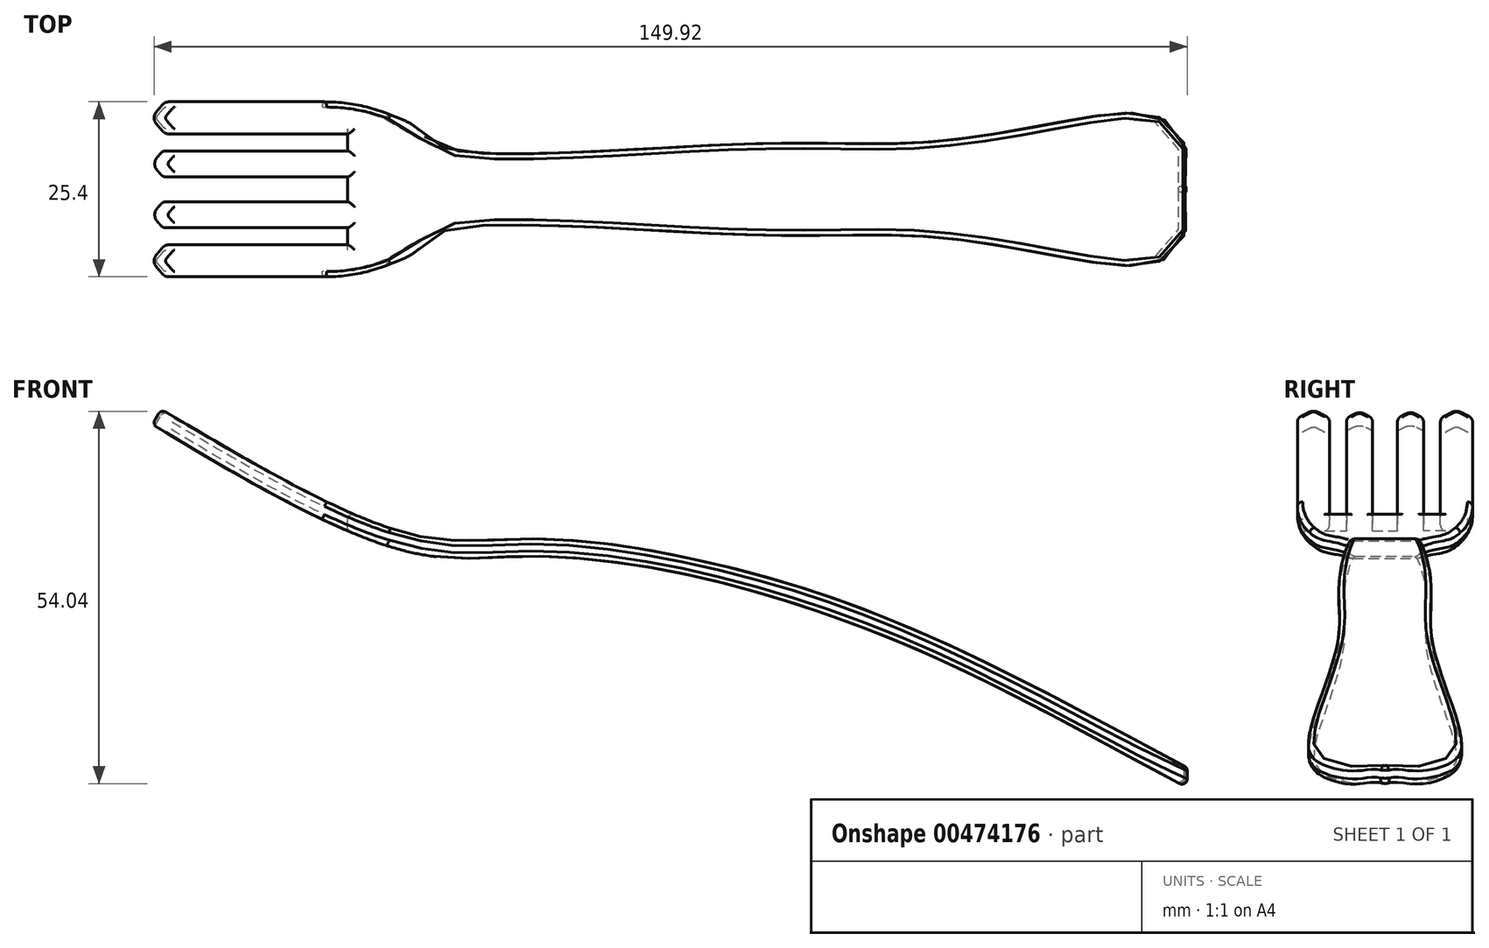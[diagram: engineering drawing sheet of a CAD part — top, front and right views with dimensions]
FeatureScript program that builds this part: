
annotation { "Feature Type Name" : "Feature", "Feature Type Description" : "" }
export const myFeature = defineFeature(function(context is Context, id is Id, definition is map)
    precondition{}
    {
        {
            var Q0;
            Q0=qCreatedBy(makeId("Front.planeOp"),FACE);
            var sketch = newSketch(context, id + "F0", { "sketchPlane" : qUnion([Q0])});
            skFitSpline(sketch, "E0", {"points": [v(0, 0) * mm, v(38.07, -18.78) * mm, v(56.38, -19.2) * mm, v(100.5, -28.62) * mm, v(152.4, -53.9) * mm], "startDerivative": vector(177.91, -105.76) * mm, "endDerivative": vector(174.38, -91.47) * mm});
            skFitSpline(sketch, "E1.0", {"points": [v(-1.3, -2.18) * mm, v(2.41, -4.39) * mm, v(9.57, -8.63) * mm, v(17.82, -13.23) * mm, v(23.97, -16.32) * mm, v(28.35, -18.3) * mm, v(31.8, -19.64) * mm, v(34.47, -20.5) * mm, v(36.4, -21.03) * mm, v(38.3, -21.44) * mm, v(40.11, -21.72) * mm, v(41.87, -21.9) * mm, v(44.14, -22) * mm, v(46.88, -21.98) * mm, v(50.14, -21.83) * mm, v(53.51, -21.7) * mm, v(57.17, -21.72) * mm, v(61.32, -22) * mm, v(67.41, -22.7) * mm, v(75.87, -24.15) * mm, v(84.97, -26.35) * mm, v(92.37, -28.52) * mm, v(97.9, -30.35) * mm, v(103.35, -32.38) * mm, v(110.52, -35.32) * mm, v(119.33, -39.4) * mm, v(129.83, -44.75) * mm, v(140.4, -50.4) * mm, v(147.57, -54.24) * mm, v(151.22, -56.16) * mm]});
            skLineSegment(sketch, "E2", {"start": v(-1.3, -2.18) * mm, "end": v(0, 0) * mm});
            skLineSegment(sketch, "E3", {"start": v(151.22, -56.16) * mm, "end": v(152.4, -53.9) * mm});
            skSolve(sketch);
        }
        {
            var Q0;
            Q0 = qSketchRegion(id + "F0", true);
            extrude(context, id + "F1", {"entities" : qUnion([Q0]), "depth" : 12.7 * mm});
        }
        {
            var Q0;
            Q0=qCreatedBy(makeId("Top.planeOp"),FACE);
            var sketch = newSketch(context, id + "F2", { "sketchPlane" : qUnion([Q0])});
            skPoint(sketch, "E4.10.internal.orphan", {"position": v(0, -1.8) * mm});
            skLineSegment(sketch, "E5.bottom", {"start": v(-4.68, 0) * mm, "end": v(27.67, 0) * mm});
            skLineSegment(sketch, "E5.top", {"start": v(-4.68, -1.8) * mm, "end": v(27.67, -1.8) * mm});
            skLineSegment(sketch, "E5.left", {"start": v(-4.68, 0) * mm, "end": v(-4.68, -1.8) * mm});
            skLineSegment(sketch, "E5.right", {"start": v(27.67, 0) * mm, "end": v(27.67, -1.8) * mm});
            skLineSegment(sketch, "E6.bottom", {"start": v(-5.34, -5.59) * mm, "end": v(27.67, -5.59) * mm});
            skLineSegment(sketch, "E6.top", {"start": v(-5.34, -8.05) * mm, "end": v(27.67, -8.05) * mm});
            skLineSegment(sketch, "E6.left", {"start": v(-5.34, -5.59) * mm, "end": v(-5.34, -8.05) * mm});
            skLineSegment(sketch, "E6.right", {"start": v(27.67, -5.59) * mm, "end": v(27.67, -8.05) * mm});
            skFitSpline(sketch, "E7", {"points": [v(149.68, 0) * mm, v(149.52, -4.1) * mm, v(147.88, -8.7) * mm, v(143.44, -11) * mm, v(129, -9.36) * mm, v(110.27, -6.74) * mm, v(84.82, -6.57) * mm, v(40.97, -6.24) * mm, v(36.87, -9.53) * mm, v(30.46, -13.47) * mm, v(147.38, -31.7) * mm, v(172.5, -1.97) * mm, v(149.68, 0) * mm]});
            skSolve(sketch);
        }
        {
            var Q0;
            Q0 = qSketchRegion(id + "F2", true);
            extrude(context, id + "F3", {"entities" : qUnion([Q0]), "operationType" : NewBodyOperationType.REMOVE, "oppositeDirection" : true, "depth" : 67.56 * mm});
        }
        {
            var Q0;
            Q0=makeQuery(id+"F1.opExtrude","SWEPT_BODY",BODY,{"disambiguationData":[OSD([sQuery(id+"F0.wireOp",EDGE,"E0"),sQuery(id+"F0.wireOp",EDGE,"E1.0"),sQuery(id+"F0.wireOp",EDGE,"E2"),sQuery(id+"F0.wireOp",EDGE,"E3")])]});
            var Q1;
            Q1=qCreatedBy(makeId("Front.planeOp"),FACE);
            mirror(context, id + "F4", {"operationType" : NewBodyOperationType.ADD, "entities" : qUnion([Q0]), "mirrorPlane" : qUnion([Q1])});
        }
        {
            var Q0;
            Q0=makeQuery(id+"F3.boolean.opBoolean","INTERSECT",EDGE,{"derivedFrom":[makeQuery(id+"F1.opExtrude","CAP_FACE",FACE,{"disambiguationData":[OSD([sQuery(id+"F0.wireOp",EDGE,"E0"),sQuery(id+"F0.wireOp",EDGE,"E1.0"),sQuery(id+"F0.wireOp",EDGE,"E2"),sQuery(id+"F0.wireOp",EDGE,"E3")])],"isStart":false}),makeQuery(id+"F3.opExtrude","SWEPT_FACE",FACE,{"disambiguationData":[OSD([sQuery(id+"F2.wireOp",EDGE,"E7")])]})]});
            var Q1;
            Q1=makeQuery(id+"F4.opPattern","COPY",EDGE,{"derivedFrom":makeQuery(id+"F3.boolean.opBoolean","INTERSECT",EDGE,{"derivedFrom":[makeQuery(id+"F1.opExtrude","CAP_FACE",FACE,{"disambiguationData":[OSD([sQuery(id+"F0.wireOp",EDGE,"E0"),sQuery(id+"F0.wireOp",EDGE,"E1.0"),sQuery(id+"F0.wireOp",EDGE,"E2"),sQuery(id+"F0.wireOp",EDGE,"E3")])],"isStart":false}),makeQuery(id+"F3.opExtrude","SWEPT_FACE",FACE,{"disambiguationData":[OSD([sQuery(id+"F2.wireOp",EDGE,"E7")])]})]}),"instanceName":"1"});
            fillet(context, id + "F5", {"entities" : qUnion([Q0, Q1]), "radius" : 25.4 * mm, "tangentPropagation" : true, "allowEdgeOverflow" : false});
        }
        {
            var Q0;
            Q0=makeQuery(id+"F4.opPattern","COPY",EDGE,{"derivedFrom":makeQuery(id+"F1.opExtrude","CAP_EDGE",EDGE,{"disambiguationData":[OSD([sQuery(id+"F0.wireOp",EDGE,"E2")])],"isStart":false}),"instanceName":"1"});
            var Q1;
            Q1=makeQuery(id+"F4.opPattern","COPY",EDGE,{"derivedFrom":makeQuery(id+"F3.boolean.opBoolean","INTERSECT",EDGE,{"derivedFrom":[makeQuery(id+"F1.opExtrude","SWEPT_FACE",FACE,{"disambiguationData":[OSD([sQuery(id+"F0.wireOp",EDGE,"E2")])]}),makeQuery(id+"F3.opExtrude","SWEPT_FACE",FACE,{"disambiguationData":[OSD([sQuery(id+"F2.wireOp",EDGE,"E6.top")])]})]}),"instanceName":"1"});
            var Q2;
            Q2=makeQuery(id+"F4.opPattern","COPY",EDGE,{"derivedFrom":makeQuery(id+"F3.boolean.opBoolean","INTERSECT",EDGE,{"derivedFrom":[makeQuery(id+"F1.opExtrude","SWEPT_FACE",FACE,{"disambiguationData":[OSD([sQuery(id+"F0.wireOp",EDGE,"E2")])]}),makeQuery(id+"F3.opExtrude","SWEPT_FACE",FACE,{"disambiguationData":[OSD([sQuery(id+"F2.wireOp",EDGE,"E6.bottom")])]})]}),"instanceName":"1"});
            var Q3;
            Q3=makeQuery(id+"F4.opPattern","COPY",EDGE,{"derivedFrom":makeQuery(id+"F3.boolean.opBoolean","INTERSECT",EDGE,{"derivedFrom":[makeQuery(id+"F1.opExtrude","SWEPT_FACE",FACE,{"disambiguationData":[OSD([sQuery(id+"F0.wireOp",EDGE,"E2")])]}),makeQuery(id+"F3.opExtrude","SWEPT_FACE",FACE,{"disambiguationData":[OSD([sQuery(id+"F2.wireOp",EDGE,"E5.top")])]})]}),"instanceName":"1"});
            var Q4;
            Q4=makeQuery(id+"F3.boolean.opBoolean","INTERSECT",EDGE,{"derivedFrom":[makeQuery(id+"F1.opExtrude","SWEPT_FACE",FACE,{"disambiguationData":[OSD([sQuery(id+"F0.wireOp",EDGE,"E2")])]}),makeQuery(id+"F3.opExtrude","SWEPT_FACE",FACE,{"disambiguationData":[OSD([sQuery(id+"F2.wireOp",EDGE,"E5.top")])]})]});
            var Q5;
            Q5=makeQuery(id+"F3.boolean.opBoolean","INTERSECT",EDGE,{"derivedFrom":[makeQuery(id+"F1.opExtrude","SWEPT_FACE",FACE,{"disambiguationData":[OSD([sQuery(id+"F0.wireOp",EDGE,"E2")])]}),makeQuery(id+"F3.opExtrude","SWEPT_FACE",FACE,{"disambiguationData":[OSD([sQuery(id+"F2.wireOp",EDGE,"E6.bottom")])]})]});
            var Q6;
            Q6=makeQuery(id+"F3.boolean.opBoolean","INTERSECT",EDGE,{"derivedFrom":[makeQuery(id+"F1.opExtrude","SWEPT_FACE",FACE,{"disambiguationData":[OSD([sQuery(id+"F0.wireOp",EDGE,"E2")])]}),makeQuery(id+"F3.opExtrude","SWEPT_FACE",FACE,{"disambiguationData":[OSD([sQuery(id+"F2.wireOp",EDGE,"E6.top")])]})]});
            var Q7;
            Q7=makeQuery(id+"F1.opExtrude","CAP_EDGE",EDGE,{"disambiguationData":[OSD([sQuery(id+"F0.wireOp",EDGE,"E2")])],"isStart":false});
            chamfer(context, id + "F6", {"entities" : qUnion([Q0, Q1, Q2, Q3, Q4, Q5, Q6, Q7]), "width" : 2.54 * mm, "tangentPropagation" : true});
        }
        {
            var Q0;
            {var subQ0=sQuery(id+"F0.wireOp",EDGE,"E2");Q0=makeQuery(id+"F6.opChamfer","BLEND_EDGE",EDGE,{"blendedFrom":[makeQuery(id+"F4.opPattern","COPY",EDGE,{"derivedFrom":makeQuery(id+"F1.opExtrude","CAP_EDGE",EDGE,{"disambiguationData":[OSD([subQ0])],"isStart":false}),"instanceName":"1"}),makeQuery(id+"F4.opPattern","COPY",EDGE,{"derivedFrom":makeQuery(id+"F3.boolean.opBoolean","INTERSECT",EDGE,{"derivedFrom":[makeQuery(id+"F1.opExtrude","SWEPT_FACE",FACE,{"disambiguationData":[OSD([subQ0])]}),makeQuery(id+"F3.opExtrude","SWEPT_FACE",FACE,{"disambiguationData":[OSD([sQuery(id+"F2.wireOp",EDGE,"E6.top")])]})]}),"instanceName":"1"})],"blendedInto":[]});}
            var Q1;
            {var subQ0=makeQuery(id+"F3.opExtrude","SWEPT_FACE",FACE,{"disambiguationData":[OSD([sQuery(id+"F2.wireOp",EDGE,"E6.top")])]});Q1=makeQuery(id+"F6.opChamfer","BLEND_EDGE",EDGE,{"blendedFrom":[makeQuery(id+"F4.opPattern","COPY",EDGE,{"derivedFrom":makeQuery(id+"F3.boolean.opBoolean","INTERSECT",EDGE,{"derivedFrom":[makeQuery(id+"F1.opExtrude","SWEPT_FACE",FACE,{"disambiguationData":[OSD([sQuery(id+"F0.wireOp",EDGE,"E2")])]}),subQ0]}),"instanceName":"1"}),makeQuery(id+"F4.opPattern","COPY",FACE,{"derivedFrom":makeQuery(id+"F3.boolean.opBoolean","COPY",FACE,{"derivedFrom":subQ0}),"instanceName":"1"})],"blendedInto":[makeQuery(id+"F4.opPattern","COPY",FACE,{"derivedFrom":makeQuery(id+"F3.boolean.opBoolean","COPY",FACE,{"derivedFrom":subQ0}),"instanceName":"1"})]});}
            var Q2;
            {var subQ0=sQuery(id+"F0.wireOp",EDGE,"E2");Q2=makeQuery(id+"F6.opChamfer","BLEND_EDGE",EDGE,{"blendedFrom":[makeQuery(id+"F4.opPattern","COPY",EDGE,{"derivedFrom":makeQuery(id+"F1.opExtrude","CAP_EDGE",EDGE,{"disambiguationData":[OSD([subQ0])],"isStart":false}),"instanceName":"1"}),makeQuery(id+"F4.opPattern","COPY",FACE,{"derivedFrom":makeQuery(id+"F1.opExtrude","CAP_FACE",FACE,{"disambiguationData":[OSD([sQuery(id+"F0.wireOp",EDGE,"E0"),sQuery(id+"F0.wireOp",EDGE,"E1.0"),subQ0,sQuery(id+"F0.wireOp",EDGE,"E3")])],"isStart":false}),"instanceName":"1"})],"blendedInto":[makeQuery(id+"F4.opPattern","COPY",FACE,{"derivedFrom":makeQuery(id+"F1.opExtrude","CAP_FACE",FACE,{"disambiguationData":[OSD([sQuery(id+"F0.wireOp",EDGE,"E0"),sQuery(id+"F0.wireOp",EDGE,"E1.0"),subQ0,sQuery(id+"F0.wireOp",EDGE,"E3")])],"isStart":false}),"instanceName":"1"})]});}
            var Q3;
            {var subQ0=makeQuery(id+"F3.opExtrude","SWEPT_FACE",FACE,{"disambiguationData":[OSD([sQuery(id+"F2.wireOp",EDGE,"E6.bottom")])]});Q3=makeQuery(id+"F6.opChamfer","BLEND_EDGE",EDGE,{"blendedFrom":[makeQuery(id+"F4.opPattern","COPY",EDGE,{"derivedFrom":makeQuery(id+"F3.boolean.opBoolean","INTERSECT",EDGE,{"derivedFrom":[makeQuery(id+"F1.opExtrude","SWEPT_FACE",FACE,{"disambiguationData":[OSD([sQuery(id+"F0.wireOp",EDGE,"E2")])]}),subQ0]}),"instanceName":"1"}),makeQuery(id+"F4.opPattern","COPY",FACE,{"derivedFrom":makeQuery(id+"F3.boolean.opBoolean","COPY",FACE,{"derivedFrom":subQ0}),"instanceName":"1"})],"blendedInto":[makeQuery(id+"F4.opPattern","COPY",FACE,{"derivedFrom":makeQuery(id+"F3.boolean.opBoolean","COPY",FACE,{"derivedFrom":subQ0}),"instanceName":"1"})]});}
            var Q4;
            {var subQ0=makeQuery(id+"F1.opExtrude","SWEPT_FACE",FACE,{"disambiguationData":[OSD([sQuery(id+"F0.wireOp",EDGE,"E2")])]});Q4=makeQuery(id+"F6.opChamfer","BLEND_EDGE",EDGE,{"blendedFrom":[makeQuery(id+"F4.opPattern","COPY",EDGE,{"derivedFrom":makeQuery(id+"F3.boolean.opBoolean","INTERSECT",EDGE,{"derivedFrom":[subQ0,makeQuery(id+"F3.opExtrude","SWEPT_FACE",FACE,{"disambiguationData":[OSD([sQuery(id+"F2.wireOp",EDGE,"E5.top")])]})]}),"instanceName":"1"}),makeQuery(id+"F4.opPattern","COPY",EDGE,{"derivedFrom":makeQuery(id+"F3.boolean.opBoolean","INTERSECT",EDGE,{"derivedFrom":[subQ0,makeQuery(id+"F3.opExtrude","SWEPT_FACE",FACE,{"disambiguationData":[OSD([sQuery(id+"F2.wireOp",EDGE,"E6.bottom")])]})]}),"instanceName":"1"})],"blendedInto":[]});}
            var Q5;
            {var subQ0=makeQuery(id+"F3.opExtrude","SWEPT_FACE",FACE,{"disambiguationData":[OSD([sQuery(id+"F2.wireOp",EDGE,"E5.top")])]});Q5=makeQuery(id+"F6.opChamfer","BLEND_EDGE",EDGE,{"blendedFrom":[makeQuery(id+"F4.opPattern","COPY",EDGE,{"derivedFrom":makeQuery(id+"F3.boolean.opBoolean","INTERSECT",EDGE,{"derivedFrom":[makeQuery(id+"F1.opExtrude","SWEPT_FACE",FACE,{"disambiguationData":[OSD([sQuery(id+"F0.wireOp",EDGE,"E2")])]}),subQ0]}),"instanceName":"1"}),makeQuery(id+"F4.opPattern","COPY",FACE,{"derivedFrom":makeQuery(id+"F3.boolean.opBoolean","COPY",FACE,{"derivedFrom":subQ0}),"instanceName":"1"})],"blendedInto":[makeQuery(id+"F4.opPattern","COPY",FACE,{"derivedFrom":makeQuery(id+"F3.boolean.opBoolean","COPY",FACE,{"derivedFrom":subQ0}),"instanceName":"1"})]});}
            var Q6;
            {var subQ0=makeQuery(id+"F3.opExtrude","SWEPT_FACE",FACE,{"disambiguationData":[OSD([sQuery(id+"F2.wireOp",EDGE,"E5.top")])]});Q6=makeQuery(id+"F6.opChamfer","BLEND_EDGE",EDGE,{"blendedFrom":[makeQuery(id+"F3.boolean.opBoolean","INTERSECT",EDGE,{"derivedFrom":[makeQuery(id+"F1.opExtrude","SWEPT_FACE",FACE,{"disambiguationData":[OSD([sQuery(id+"F0.wireOp",EDGE,"E2")])]}),subQ0]}),makeQuery(id+"F3.boolean.opBoolean","COPY",FACE,{"derivedFrom":subQ0})],"blendedInto":[makeQuery(id+"F3.boolean.opBoolean","COPY",FACE,{"derivedFrom":subQ0})]});}
            var Q7;
            {var subQ0=makeQuery(id+"F1.opExtrude","SWEPT_FACE",FACE,{"disambiguationData":[OSD([sQuery(id+"F0.wireOp",EDGE,"E2")])]});Q7=makeQuery(id+"F6.opChamfer","BLEND_EDGE",EDGE,{"blendedFrom":[makeQuery(id+"F3.boolean.opBoolean","INTERSECT",EDGE,{"derivedFrom":[subQ0,makeQuery(id+"F3.opExtrude","SWEPT_FACE",FACE,{"disambiguationData":[OSD([sQuery(id+"F2.wireOp",EDGE,"E5.top")])]})]}),makeQuery(id+"F3.boolean.opBoolean","INTERSECT",EDGE,{"derivedFrom":[subQ0,makeQuery(id+"F3.opExtrude","SWEPT_FACE",FACE,{"disambiguationData":[OSD([sQuery(id+"F2.wireOp",EDGE,"E6.bottom")])]})]})],"blendedInto":[]});}
            var Q8;
            {var subQ0=makeQuery(id+"F3.opExtrude","SWEPT_FACE",FACE,{"disambiguationData":[OSD([sQuery(id+"F2.wireOp",EDGE,"E6.bottom")])]});Q8=makeQuery(id+"F6.opChamfer","BLEND_EDGE",EDGE,{"blendedFrom":[makeQuery(id+"F3.boolean.opBoolean","INTERSECT",EDGE,{"derivedFrom":[makeQuery(id+"F1.opExtrude","SWEPT_FACE",FACE,{"disambiguationData":[OSD([sQuery(id+"F0.wireOp",EDGE,"E2")])]}),subQ0]}),makeQuery(id+"F3.boolean.opBoolean","COPY",FACE,{"derivedFrom":subQ0})],"blendedInto":[makeQuery(id+"F3.boolean.opBoolean","COPY",FACE,{"derivedFrom":subQ0})]});}
            var Q9;
            {var subQ0=makeQuery(id+"F3.opExtrude","SWEPT_FACE",FACE,{"disambiguationData":[OSD([sQuery(id+"F2.wireOp",EDGE,"E6.top")])]});Q9=makeQuery(id+"F6.opChamfer","BLEND_EDGE",EDGE,{"blendedFrom":[makeQuery(id+"F3.boolean.opBoolean","INTERSECT",EDGE,{"derivedFrom":[makeQuery(id+"F1.opExtrude","SWEPT_FACE",FACE,{"disambiguationData":[OSD([sQuery(id+"F0.wireOp",EDGE,"E2")])]}),subQ0]}),makeQuery(id+"F3.boolean.opBoolean","COPY",FACE,{"derivedFrom":subQ0})],"blendedInto":[makeQuery(id+"F3.boolean.opBoolean","COPY",FACE,{"derivedFrom":subQ0})]});}
            var Q10;
            {var subQ0=sQuery(id+"F0.wireOp",EDGE,"E2");Q10=makeQuery(id+"F6.opChamfer","BLEND_EDGE",EDGE,{"blendedFrom":[makeQuery(id+"F1.opExtrude","CAP_EDGE",EDGE,{"disambiguationData":[OSD([subQ0])],"isStart":false}),makeQuery(id+"F3.boolean.opBoolean","INTERSECT",EDGE,{"derivedFrom":[makeQuery(id+"F1.opExtrude","SWEPT_FACE",FACE,{"disambiguationData":[OSD([subQ0])]}),makeQuery(id+"F3.opExtrude","SWEPT_FACE",FACE,{"disambiguationData":[OSD([sQuery(id+"F2.wireOp",EDGE,"E6.top")])]})]})],"blendedInto":[]});}
            var Q11;
            {var subQ0=sQuery(id+"F0.wireOp",EDGE,"E2");Q11=makeQuery(id+"F6.opChamfer","BLEND_EDGE",EDGE,{"blendedFrom":[makeQuery(id+"F1.opExtrude","CAP_EDGE",EDGE,{"disambiguationData":[OSD([subQ0])],"isStart":false}),makeQuery(id+"F1.opExtrude","CAP_FACE",FACE,{"disambiguationData":[OSD([sQuery(id+"F0.wireOp",EDGE,"E0"),sQuery(id+"F0.wireOp",EDGE,"E1.0"),subQ0,sQuery(id+"F0.wireOp",EDGE,"E3")])],"isStart":false})],"blendedInto":[makeQuery(id+"F1.opExtrude","CAP_FACE",FACE,{"disambiguationData":[OSD([sQuery(id+"F0.wireOp",EDGE,"E0"),sQuery(id+"F0.wireOp",EDGE,"E1.0"),subQ0,sQuery(id+"F0.wireOp",EDGE,"E3")])],"isStart":false})]});}
            var Q12;
            {var subQ0=makeQuery(id+"F3.boolean.opBoolean","INTERSECT",EDGE,{"derivedFrom":[makeQuery(id+"F1.opExtrude","CAP_FACE",FACE,{"disambiguationData":[OSD([sQuery(id+"F0.wireOp",EDGE,"E0"),sQuery(id+"F0.wireOp",EDGE,"E1.0"),sQuery(id+"F0.wireOp",EDGE,"E2"),sQuery(id+"F0.wireOp",EDGE,"E3")])],"isStart":true}),makeQuery(id+"F3.opExtrude","SWEPT_FACE",FACE,{"disambiguationData":[OSD([sQuery(id+"F2.wireOp",EDGE,"E7")])]})]});Q12=makeQuery(id+"F4.boolean.opBoolean","MERGE",EDGE,{"derivedFrom":[subQ0,makeQuery(id+"F4.opPattern","COPY",EDGE,{"derivedFrom":subQ0,"instanceName":"1"})]});}
            fillet(context, id + "F7", {"entities" : qUnion([Q0, Q1, Q2, Q3, Q4, Q5, Q6, Q7, Q8, Q9, Q10, Q11, Q12]), "radius" : 1.27 * mm, "tangentPropagation" : true, "allowEdgeOverflow" : false});
        }
        {
            var Q0;
            Q0=makeQuery(id+"F3.boolean.opBoolean","INTERSECT",EDGE,{"derivedFrom":[makeQuery(id+"F1.opExtrude","SWEPT_FACE",FACE,{"disambiguationData":[OSD([sQuery(id+"F0.wireOp",EDGE,"E0")])]}),makeQuery(id+"F3.opExtrude","SWEPT_FACE",FACE,{"disambiguationData":[OSD([sQuery(id+"F2.wireOp",EDGE,"E7")])]})]});
            var Q1;
            Q1=makeQuery(id+"F1.opExtrude","CAP_EDGE",EDGE,{"disambiguationData":[OSD([sQuery(id+"F0.wireOp",EDGE,"E0")])],"isStart":false});
            var Q2;
            {var subQ0=makeQuery(id+"F1.opExtrude","SWEPT_FACE",FACE,{"disambiguationData":[OSD([sQuery(id+"F0.wireOp",EDGE,"E0")])]});Q2=makeQuery(id+"F4.boolean.opBoolean","MERGE",FACE,{"derivedFrom":[subQ0,makeQuery(id+"F4.opPattern","COPY",FACE,{"derivedFrom":subQ0,"instanceName":"1"})]});}
            var Q3;
            Q3=makeQuery(id+"F3.boolean.opBoolean","INTERSECT",EDGE,{"derivedFrom":[makeQuery(id+"F1.opExtrude","SWEPT_FACE",FACE,{"disambiguationData":[OSD([sQuery(id+"F0.wireOp",EDGE,"E1.0")])]}),makeQuery(id+"F3.opExtrude","SWEPT_FACE",FACE,{"disambiguationData":[OSD([sQuery(id+"F2.wireOp",EDGE,"E7")])]})]});
            fillet(context, id + "F8", {"entities" : qUnion([Q0, Q1, Q2, Q3]), "radius" : 0.76 * mm, "tangentPropagation" : true, "allowEdgeOverflow" : false});
        }
    });
